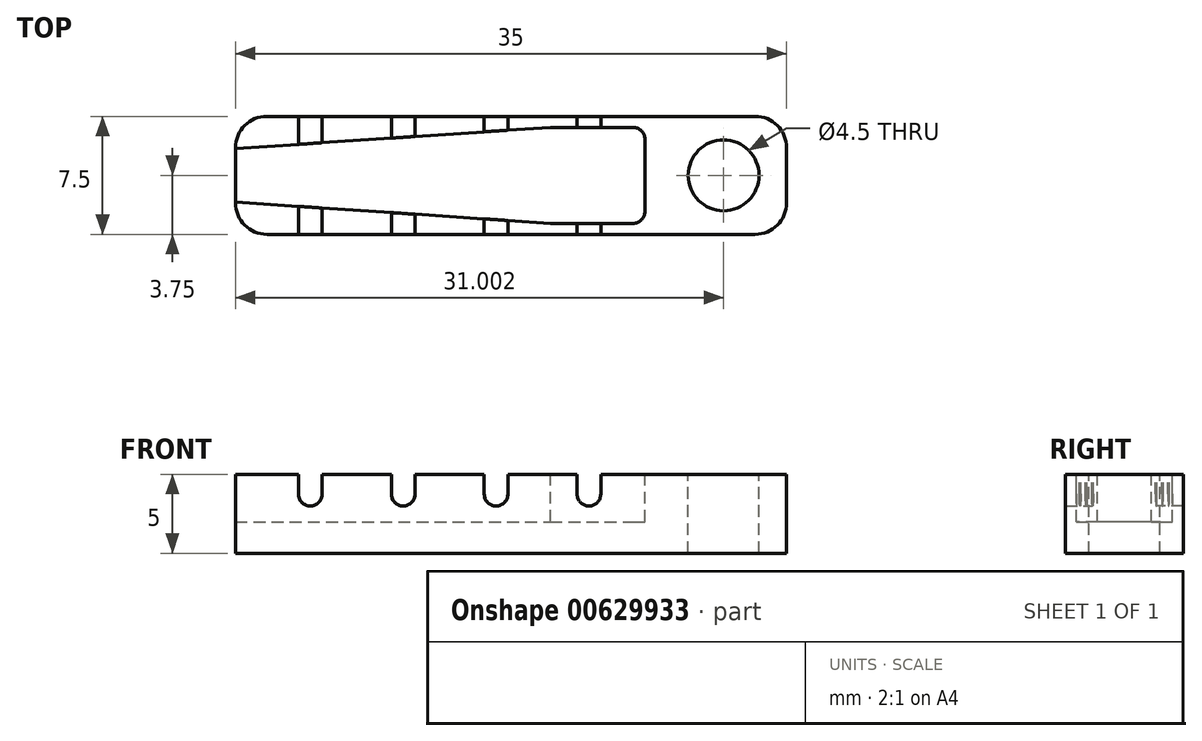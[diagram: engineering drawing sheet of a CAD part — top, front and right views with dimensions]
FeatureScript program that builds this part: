
annotation { "Feature Type Name" : "Feature", "Feature Type Description" : "" }
export const myFeature = defineFeature(function(context is Context, id is Id, definition is map)
    precondition{}
    {
        {
            var Q0;
            Q0=qCreatedBy(makeId("Top.planeOp"),FACE);
            var sketch = newSketch(context, id + "F0", { "sketchPlane" : qUnion([Q0])});
            skLineSegment(sketch, "E0.bottom", {"start": v(-22.89, 3.75) * mm, "end": v(12.11, 3.75) * mm});
            skLineSegment(sketch, "E0.top", {"start": v(-22.89, -3.75) * mm, "end": v(12.11, -3.75) * mm});
            skLineSegment(sketch, "E0.left", {"start": v(-22.89, 3.75) * mm, "end": v(-22.89, -3.75) * mm});
            skLineSegment(sketch, "E0.right", {"start": v(12.11, 3.75) * mm, "end": v(12.11, -3.75) * mm});
            skLineSegment(sketch, "E1", {"start": v(-22.89, 1.7) * mm, "end": v(-2.89, 3.05) * mm});
            skLineSegment(sketch, "E2.MirrorCS", {"start": v(-22.89, -1.7) * mm, "end": v(-2.89, -3.05) * mm});
            skLineSegment(sketch, "E3", {"start": v(-2.89, 3.05) * mm, "end": v(3.11, 3.05) * mm});
            skLineSegment(sketch, "E4.MirrorCS", {"start": v(-2.89, -3.05) * mm, "end": v(3.11, -3.05) * mm});
            skLineSegment(sketch, "E5", {"start": v(3.11, 3.05) * mm, "end": v(3.11, -3.05) * mm});
            skCircle(sketch, "E6", {"center": v(8.11, 0) * mm, "radius": 2.25 * mm});
            skLineSegment(sketch, "E7", {"start": v(-18.89, 3.75) * mm, "end": v(-18.89, -3.75) * mm});
            skLineSegment(sketch, "E8", {"start": v(-17.39, 3.75) * mm, "end": v(-17.39, -3.75) * mm});
            skLineSegment(sketch, "E9.1.0.0", {"start": v(-12.99, 3.75) * mm, "end": v(-12.99, -3.75) * mm});
            skLineSegment(sketch, "E9.1.0.1", {"start": v(-11.49, 3.75) * mm, "end": v(-11.49, -3.75) * mm});
            skLineSegment(sketch, "E9.2.0.0", {"start": v(-7.09, 3.75) * mm, "end": v(-7.09, -3.75) * mm});
            skLineSegment(sketch, "E9.2.0.1", {"start": v(-5.59, 3.75) * mm, "end": v(-5.59, -3.75) * mm});
            skLineSegment(sketch, "E9.3.0.0", {"start": v(-1.19, 3.75) * mm, "end": v(-1.19, -3.75) * mm});
            skLineSegment(sketch, "E9.3.0.1", {"start": v(0.31, 3.75) * mm, "end": v(0.31, -3.75) * mm});
            skLineSegment(sketch, "E9.direction1", {"start": v(-18.89, -3.75) * mm, "end": v(-12.99, -3.75) * mm, "construction": true});
            skSolve(sketch);
        }
        {
            var Q0;
            Q0=qSketchRegion(id+"F0",true);
            var Q1;
            {var subQ0=sQuery(id+"F0.wireOp",EDGE,"E9.3.0.0");var subQ1=sQuery(id+"F0.wireOp",EDGE,"E3");var subQ2=makeQuery(id+"F0.imprint","INTERSECT",VERTEX,{"derivedFrom":[subQ1,subQ0]});Q1=makeQuery(id+"F0.imprint","IMPRINT",FACE,{"disambiguationData":[TD([[makeQuery(id+"F0.imprint","IMPRINT",EDGE,{"disambiguationData":[TD([[subQ2,-1.0]])],"derivedFrom":subQ1}),-1.0]])]});}
            var Q2;
            {var subQ0=sQuery(id+"F0.wireOp",EDGE,"E9.2.0.0");var subQ1=sQuery(id+"F0.wireOp",EDGE,"E1");var subQ2=makeQuery(id+"F0.imprint","INTERSECT",VERTEX,{"derivedFrom":[subQ1,subQ0]});Q2=makeQuery(id+"F0.imprint","IMPRINT",FACE,{"disambiguationData":[TD([[makeQuery(id+"F0.imprint","IMPRINT",EDGE,{"disambiguationData":[TD([[subQ2,-1.0]])],"derivedFrom":subQ1}),-1.0]])]});}
            var Q3;
            {var subQ0=sQuery(id+"F0.wireOp",EDGE,"E7");var subQ1=sQuery(id+"F0.wireOp",EDGE,"E1");var subQ2=makeQuery(id+"F0.imprint","INTERSECT",VERTEX,{"derivedFrom":[subQ1,subQ0]});Q3=makeQuery(id+"F0.imprint","IMPRINT",FACE,{"disambiguationData":[TD([[makeQuery(id+"F0.imprint","IMPRINT",EDGE,{"disambiguationData":[TD([[subQ2,-1.0]])],"derivedFrom":subQ1}),-1.0]])]});}
            var Q4;
            {var subQ0=sQuery(id+"F0.wireOp",EDGE,"E8");var subQ1=sQuery(id+"F0.wireOp",EDGE,"E1");var subQ2=makeQuery(id+"F0.imprint","INTERSECT",VERTEX,{"derivedFrom":[subQ1,subQ0]});Q4=makeQuery(id+"F0.imprint","IMPRINT",FACE,{"disambiguationData":[TD([[makeQuery(id+"F0.imprint","IMPRINT",EDGE,{"disambiguationData":[TD([[subQ2,-1.0]])],"derivedFrom":subQ1}),-1.0]])]});}
            var Q5;
            {var subQ0=sQuery(id+"F0.wireOp",EDGE,"E9.1.0.1");var subQ1=sQuery(id+"F0.wireOp",EDGE,"E1");var subQ2=makeQuery(id+"F0.imprint","INTERSECT",VERTEX,{"derivedFrom":[subQ1,subQ0]});Q5=makeQuery(id+"F0.imprint","IMPRINT",FACE,{"disambiguationData":[TD([[makeQuery(id+"F0.imprint","IMPRINT",EDGE,{"disambiguationData":[TD([[subQ2,-1.0]])],"derivedFrom":subQ1}),-1.0]])]});}
            var Q6;
            {var subQ0=sQuery(id+"F0.wireOp",EDGE,"E9.1.0.0");var subQ1=sQuery(id+"F0.wireOp",EDGE,"E1");var subQ2=makeQuery(id+"F0.imprint","INTERSECT",VERTEX,{"derivedFrom":[subQ1,subQ0]});Q6=makeQuery(id+"F0.imprint","IMPRINT",FACE,{"disambiguationData":[TD([[makeQuery(id+"F0.imprint","IMPRINT",EDGE,{"disambiguationData":[TD([[subQ2,-1.0]])],"derivedFrom":subQ1}),-1.0]])]});}
            var Q7;
            {var subQ5=sQuery(id+"F0.wireOp",EDGE,"E3");var subQ6=sQuery(id+"F0.wireOp",EDGE,"E1");var subQ7=makeQuery(id+"F0.imprint","INTERSECT",VERTEX,{"derivedFrom":[subQ6,subQ5]});Q7=makeQuery(id+"F0.imprint","IMPRINT",FACE,{"disambiguationData":[TD([[makeQuery(id+"F0.imprint","IMPRINT",EDGE,{"disambiguationData":[TD([[subQ7,1.0]])],"derivedFrom":subQ6}),-1.0]])]});}
            var Q8;
            {var subQ0=sQuery(id+"F0.wireOp",EDGE,"E5");Q8=makeQuery(id+"F0.imprint","IMPRINT",FACE,{"disambiguationData":[TD([[makeQuery(id+"F0.imprint","IMPRINT",EDGE,{"derivedFrom":subQ0}),-1.0]])]});}
            extrude(context, id + "F1", {"entities" : qUnion([Q0, Q1, Q2, Q3, Q4, Q5, Q6, Q7, Q8]), "depth" : -5 * mm, "offsetDistance" : 25 * mm});
        }
        {
            var Q0;
            {var subQ0=sQuery(id+"F0.wireOp",EDGE,"E1");var subQ1=sQuery(id+"F0.wireOp",EDGE,"E0.left");var subQ2=makeQuery(id+"F0.imprint","INTERSECT",VERTEX,{"derivedFrom":[subQ1,subQ0]});Q0=makeQuery(id+"F0.imprint","IMPRINT",FACE,{"disambiguationData":[TD([[makeQuery(id+"F0.imprint","IMPRINT",EDGE,{"disambiguationData":[TD([[subQ2,-1.0]])],"derivedFrom":subQ1}),1.0]])]});}
            var Q1;
            {var subQ0=sQuery(id+"F0.wireOp",EDGE,"E7");var subQ1=sQuery(id+"F0.wireOp",EDGE,"E1");var subQ2=makeQuery(id+"F0.imprint","INTERSECT",VERTEX,{"derivedFrom":[subQ1,subQ0]});Q1=makeQuery(id+"F0.imprint","IMPRINT",FACE,{"disambiguationData":[TD([[makeQuery(id+"F0.imprint","IMPRINT",EDGE,{"disambiguationData":[TD([[subQ2,-1.0]])],"derivedFrom":subQ1}),-1.0]])]});}
            var Q2;
            {var subQ0=sQuery(id+"F0.wireOp",EDGE,"E8");var subQ1=sQuery(id+"F0.wireOp",EDGE,"E1");var subQ2=makeQuery(id+"F0.imprint","INTERSECT",VERTEX,{"derivedFrom":[subQ1,subQ0]});Q2=makeQuery(id+"F0.imprint","IMPRINT",FACE,{"disambiguationData":[TD([[makeQuery(id+"F0.imprint","IMPRINT",EDGE,{"disambiguationData":[TD([[subQ2,-1.0]])],"derivedFrom":subQ1}),-1.0]])]});}
            var Q3;
            {var subQ0=sQuery(id+"F0.wireOp",EDGE,"E9.1.0.0");var subQ1=sQuery(id+"F0.wireOp",EDGE,"E1");var subQ2=makeQuery(id+"F0.imprint","INTERSECT",VERTEX,{"derivedFrom":[subQ1,subQ0]});Q3=makeQuery(id+"F0.imprint","IMPRINT",FACE,{"disambiguationData":[TD([[makeQuery(id+"F0.imprint","IMPRINT",EDGE,{"disambiguationData":[TD([[subQ2,-1.0]])],"derivedFrom":subQ1}),-1.0]])]});}
            var Q4;
            {var subQ0=sQuery(id+"F0.wireOp",EDGE,"E9.1.0.1");var subQ1=sQuery(id+"F0.wireOp",EDGE,"E1");var subQ2=makeQuery(id+"F0.imprint","INTERSECT",VERTEX,{"derivedFrom":[subQ1,subQ0]});Q4=makeQuery(id+"F0.imprint","IMPRINT",FACE,{"disambiguationData":[TD([[makeQuery(id+"F0.imprint","IMPRINT",EDGE,{"disambiguationData":[TD([[subQ2,-1.0]])],"derivedFrom":subQ1}),-1.0]])]});}
            var Q5;
            {var subQ0=sQuery(id+"F0.wireOp",EDGE,"E9.2.0.0");var subQ1=sQuery(id+"F0.wireOp",EDGE,"E1");var subQ2=makeQuery(id+"F0.imprint","INTERSECT",VERTEX,{"derivedFrom":[subQ1,subQ0]});Q5=makeQuery(id+"F0.imprint","IMPRINT",FACE,{"disambiguationData":[TD([[makeQuery(id+"F0.imprint","IMPRINT",EDGE,{"disambiguationData":[TD([[subQ2,-1.0]])],"derivedFrom":subQ1}),-1.0]])]});}
            var Q6;
            {var subQ5=sQuery(id+"F0.wireOp",EDGE,"E3");var subQ6=sQuery(id+"F0.wireOp",EDGE,"E1");var subQ7=makeQuery(id+"F0.imprint","INTERSECT",VERTEX,{"derivedFrom":[subQ6,subQ5]});Q6=makeQuery(id+"F0.imprint","IMPRINT",FACE,{"disambiguationData":[TD([[makeQuery(id+"F0.imprint","IMPRINT",EDGE,{"disambiguationData":[TD([[subQ7,1.0]])],"derivedFrom":subQ6}),-1.0]])]});}
            var Q7;
            {var subQ0=sQuery(id+"F0.wireOp",EDGE,"E9.3.0.0");var subQ1=sQuery(id+"F0.wireOp",EDGE,"E3");var subQ2=makeQuery(id+"F0.imprint","INTERSECT",VERTEX,{"derivedFrom":[subQ1,subQ0]});Q7=makeQuery(id+"F0.imprint","IMPRINT",FACE,{"disambiguationData":[TD([[makeQuery(id+"F0.imprint","IMPRINT",EDGE,{"disambiguationData":[TD([[subQ2,-1.0]])],"derivedFrom":subQ1}),-1.0]])]});}
            var Q8;
            {var subQ0=sQuery(id+"F0.wireOp",EDGE,"E5");Q8=makeQuery(id+"F0.imprint","IMPRINT",FACE,{"disambiguationData":[TD([[makeQuery(id+"F0.imprint","IMPRINT",EDGE,{"derivedFrom":subQ0}),-1.0]])]});}
            extrude(context, id + "F2", {"entities" : qUnion([Q0, Q1, Q2, Q3, Q4, Q5, Q6, Q7, Q8]), "operationType" : NewBodyOperationType.REMOVE, "depth" : -3 * mm, "offsetDistance" : 25 * mm});
        }
        {
            var Q0;
            {var subQ0=sQuery(id+"F0.wireOp",EDGE,"E7");var subQ1=sQuery(id+"F0.wireOp",EDGE,"E0.bottom");var subQ2=makeQuery(id+"F0.imprint","INTERSECT",VERTEX,{"derivedFrom":[subQ1,subQ0]});Q0=makeQuery(id+"F0.imprint","IMPRINT",FACE,{"disambiguationData":[TD([[makeQuery(id+"F0.imprint","IMPRINT",EDGE,{"disambiguationData":[TD([[subQ2,-1.0]])],"derivedFrom":subQ1}),-1.0]])]});}
            var Q1;
            {var subQ0=sQuery(id+"F0.wireOp",EDGE,"E9.1.0.0");var subQ1=sQuery(id+"F0.wireOp",EDGE,"E0.bottom");var subQ2=makeQuery(id+"F0.imprint","INTERSECT",VERTEX,{"derivedFrom":[subQ1,subQ0]});Q1=makeQuery(id+"F0.imprint","IMPRINT",FACE,{"disambiguationData":[TD([[makeQuery(id+"F0.imprint","IMPRINT",EDGE,{"disambiguationData":[TD([[subQ2,-1.0]])],"derivedFrom":subQ1}),-1.0]])]});}
            var Q2;
            {var subQ0=sQuery(id+"F0.wireOp",EDGE,"E9.2.0.0");var subQ1=sQuery(id+"F0.wireOp",EDGE,"E0.bottom");var subQ2=makeQuery(id+"F0.imprint","INTERSECT",VERTEX,{"derivedFrom":[subQ1,subQ0]});Q2=makeQuery(id+"F0.imprint","IMPRINT",FACE,{"disambiguationData":[TD([[makeQuery(id+"F0.imprint","IMPRINT",EDGE,{"disambiguationData":[TD([[subQ2,-1.0]])],"derivedFrom":subQ1}),-1.0]])]});}
            var Q3;
            {var subQ0=sQuery(id+"F0.wireOp",EDGE,"E9.3.0.0");var subQ1=sQuery(id+"F0.wireOp",EDGE,"E0.top");var subQ2=makeQuery(id+"F0.imprint","INTERSECT",VERTEX,{"derivedFrom":[subQ1,subQ0]});Q3=makeQuery(id+"F0.imprint","IMPRINT",FACE,{"disambiguationData":[TD([[makeQuery(id+"F0.imprint","IMPRINT",EDGE,{"disambiguationData":[TD([[subQ2,-1.0]])],"derivedFrom":subQ1}),1.0]])]});}
            var Q4;
            {var subQ0=sQuery(id+"F0.wireOp",EDGE,"E7");var subQ1=sQuery(id+"F0.wireOp",EDGE,"E0.top");var subQ2=makeQuery(id+"F0.imprint","INTERSECT",VERTEX,{"derivedFrom":[subQ1,subQ0]});Q4=makeQuery(id+"F0.imprint","IMPRINT",FACE,{"disambiguationData":[TD([[makeQuery(id+"F0.imprint","IMPRINT",EDGE,{"disambiguationData":[TD([[subQ2,-1.0]])],"derivedFrom":subQ1}),1.0]])]});}
            var Q5;
            {var subQ0=sQuery(id+"F0.wireOp",EDGE,"E9.1.0.0");var subQ1=sQuery(id+"F0.wireOp",EDGE,"E0.top");var subQ2=makeQuery(id+"F0.imprint","INTERSECT",VERTEX,{"derivedFrom":[subQ1,subQ0]});Q5=makeQuery(id+"F0.imprint","IMPRINT",FACE,{"disambiguationData":[TD([[makeQuery(id+"F0.imprint","IMPRINT",EDGE,{"disambiguationData":[TD([[subQ2,-1.0]])],"derivedFrom":subQ1}),1.0]])]});}
            var Q6;
            {var subQ0=sQuery(id+"F0.wireOp",EDGE,"E9.2.0.0");var subQ1=sQuery(id+"F0.wireOp",EDGE,"E0.top");var subQ2=makeQuery(id+"F0.imprint","INTERSECT",VERTEX,{"derivedFrom":[subQ1,subQ0]});Q6=makeQuery(id+"F0.imprint","IMPRINT",FACE,{"disambiguationData":[TD([[makeQuery(id+"F0.imprint","IMPRINT",EDGE,{"disambiguationData":[TD([[subQ2,-1.0]])],"derivedFrom":subQ1}),1.0]])]});}
            var Q7;
            {var subQ0=sQuery(id+"F0.wireOp",EDGE,"E9.3.0.0");var subQ1=sQuery(id+"F0.wireOp",EDGE,"E0.bottom");var subQ2=makeQuery(id+"F0.imprint","INTERSECT",VERTEX,{"derivedFrom":[subQ1,subQ0]});Q7=makeQuery(id+"F0.imprint","IMPRINT",FACE,{"disambiguationData":[TD([[makeQuery(id+"F0.imprint","IMPRINT",EDGE,{"disambiguationData":[TD([[subQ2,-1.0]])],"derivedFrom":subQ1}),-1.0]])]});}
            extrude(context, id + "F3", {"entities" : qUnion([Q0, Q1, Q2, Q3, Q4, Q5, Q6, Q7]), "operationType" : NewBodyOperationType.REMOVE, "oppositeDirection" : true, "depth" : 2 * mm, "offsetDistance" : 25 * mm});
        }
        {
            var Q0;
            {var subQ0=sQuery(id+"F0.wireOp",EDGE,"E8");Q0=makeQuery(id+"F3.boolean.opBoolean","COPY",EDGE,{"derivedFrom":makeQuery(id+"F3.opExtrude","CAP_EDGE",EDGE,{"disambiguationData":[OSD([subQ0]),TDD([makeQuery(id+"F0.imprint","IMPRINT",EDGE,{"disambiguationData":[TD([[makeQuery(id+"F0.imprint","INTERSECT",VERTEX,{"derivedFrom":[sQuery(id+"F0.wireOp",EDGE,"E0.top"),subQ0]}),1.0]])],"derivedFrom":subQ0})])],"isStart":false})});}
            var Q1;
            {var subQ0=sQuery(id+"F0.wireOp",EDGE,"E9.1.0.1");Q1=makeQuery(id+"F3.boolean.opBoolean","COPY",EDGE,{"derivedFrom":makeQuery(id+"F3.opExtrude","CAP_EDGE",EDGE,{"disambiguationData":[OSD([subQ0]),TDD([makeQuery(id+"F0.imprint","IMPRINT",EDGE,{"disambiguationData":[TD([[makeQuery(id+"F0.imprint","INTERSECT",VERTEX,{"derivedFrom":[sQuery(id+"F0.wireOp",EDGE,"E0.top"),subQ0]}),1.0]])],"derivedFrom":subQ0})])],"isStart":false})});}
            var Q2;
            {var subQ0=sQuery(id+"F0.wireOp",EDGE,"E9.2.0.1");Q2=makeQuery(id+"F3.boolean.opBoolean","COPY",EDGE,{"derivedFrom":makeQuery(id+"F3.opExtrude","CAP_EDGE",EDGE,{"disambiguationData":[OSD([subQ0]),TDD([makeQuery(id+"F0.imprint","IMPRINT",EDGE,{"disambiguationData":[TD([[makeQuery(id+"F0.imprint","INTERSECT",VERTEX,{"derivedFrom":[sQuery(id+"F0.wireOp",EDGE,"E0.top"),subQ0]}),1.0]])],"derivedFrom":subQ0})])],"isStart":false})});}
            var Q3;
            {var subQ0=sQuery(id+"F0.wireOp",EDGE,"E9.3.0.1");Q3=makeQuery(id+"F3.boolean.opBoolean","COPY",EDGE,{"derivedFrom":makeQuery(id+"F3.opExtrude","CAP_EDGE",EDGE,{"disambiguationData":[OSD([subQ0]),TDD([makeQuery(id+"F0.imprint","IMPRINT",EDGE,{"disambiguationData":[TD([[makeQuery(id+"F0.imprint","INTERSECT",VERTEX,{"derivedFrom":[sQuery(id+"F0.wireOp",EDGE,"E0.top"),subQ0]}),1.0]])],"derivedFrom":subQ0})])],"isStart":false})});}
            var Q4;
            {var subQ0=sQuery(id+"F0.wireOp",EDGE,"E7");Q4=makeQuery(id+"F3.boolean.opBoolean","COPY",EDGE,{"derivedFrom":makeQuery(id+"F3.opExtrude","CAP_EDGE",EDGE,{"disambiguationData":[OSD([subQ0]),TDD([makeQuery(id+"F0.imprint","IMPRINT",EDGE,{"disambiguationData":[TD([[makeQuery(id+"F0.imprint","INTERSECT",VERTEX,{"derivedFrom":[sQuery(id+"F0.wireOp",EDGE,"E0.top"),subQ0]}),1.0]])],"derivedFrom":subQ0})])],"isStart":false})});}
            var Q5;
            {var subQ0=sQuery(id+"F0.wireOp",EDGE,"E9.1.0.0");Q5=makeQuery(id+"F3.boolean.opBoolean","COPY",EDGE,{"derivedFrom":makeQuery(id+"F3.opExtrude","CAP_EDGE",EDGE,{"disambiguationData":[OSD([subQ0]),TDD([makeQuery(id+"F0.imprint","IMPRINT",EDGE,{"disambiguationData":[TD([[makeQuery(id+"F0.imprint","INTERSECT",VERTEX,{"derivedFrom":[sQuery(id+"F0.wireOp",EDGE,"E0.top"),subQ0]}),1.0]])],"derivedFrom":subQ0})])],"isStart":false})});}
            var Q6;
            {var subQ0=sQuery(id+"F0.wireOp",EDGE,"E9.2.0.0");Q6=makeQuery(id+"F3.boolean.opBoolean","COPY",EDGE,{"derivedFrom":makeQuery(id+"F3.opExtrude","CAP_EDGE",EDGE,{"disambiguationData":[OSD([subQ0]),TDD([makeQuery(id+"F0.imprint","IMPRINT",EDGE,{"disambiguationData":[TD([[makeQuery(id+"F0.imprint","INTERSECT",VERTEX,{"derivedFrom":[sQuery(id+"F0.wireOp",EDGE,"E0.top"),subQ0]}),1.0]])],"derivedFrom":subQ0})])],"isStart":false})});}
            var Q7;
            {var subQ0=sQuery(id+"F0.wireOp",EDGE,"E9.3.0.0");Q7=makeQuery(id+"F3.boolean.opBoolean","COPY",EDGE,{"derivedFrom":makeQuery(id+"F3.opExtrude","CAP_EDGE",EDGE,{"disambiguationData":[OSD([subQ0]),TDD([makeQuery(id+"F0.imprint","IMPRINT",EDGE,{"disambiguationData":[TD([[makeQuery(id+"F0.imprint","INTERSECT",VERTEX,{"derivedFrom":[sQuery(id+"F0.wireOp",EDGE,"E0.top"),subQ0]}),1.0]])],"derivedFrom":subQ0})])],"isStart":false})});}
            var Q8;
            {var subQ0=sQuery(id+"F0.wireOp",EDGE,"E7");Q8=makeQuery(id+"F3.boolean.opBoolean","COPY",EDGE,{"derivedFrom":makeQuery(id+"F3.opExtrude","CAP_EDGE",EDGE,{"disambiguationData":[OSD([subQ0]),TDD([makeQuery(id+"F0.imprint","IMPRINT",EDGE,{"disambiguationData":[TD([[makeQuery(id+"F0.imprint","INTERSECT",VERTEX,{"derivedFrom":[sQuery(id+"F0.wireOp",EDGE,"E0.bottom"),subQ0]}),-1.0]])],"derivedFrom":subQ0})])],"isStart":false})});}
            var Q9;
            {var subQ0=sQuery(id+"F0.wireOp",EDGE,"E9.1.0.0");Q9=makeQuery(id+"F3.boolean.opBoolean","COPY",EDGE,{"derivedFrom":makeQuery(id+"F3.opExtrude","CAP_EDGE",EDGE,{"disambiguationData":[OSD([subQ0]),TDD([makeQuery(id+"F0.imprint","IMPRINT",EDGE,{"disambiguationData":[TD([[makeQuery(id+"F0.imprint","INTERSECT",VERTEX,{"derivedFrom":[sQuery(id+"F0.wireOp",EDGE,"E0.bottom"),subQ0]}),-1.0]])],"derivedFrom":subQ0})])],"isStart":false})});}
            var Q10;
            {var subQ0=sQuery(id+"F0.wireOp",EDGE,"E9.2.0.0");Q10=makeQuery(id+"F3.boolean.opBoolean","COPY",EDGE,{"derivedFrom":makeQuery(id+"F3.opExtrude","CAP_EDGE",EDGE,{"disambiguationData":[OSD([subQ0]),TDD([makeQuery(id+"F0.imprint","IMPRINT",EDGE,{"disambiguationData":[TD([[makeQuery(id+"F0.imprint","INTERSECT",VERTEX,{"derivedFrom":[sQuery(id+"F0.wireOp",EDGE,"E0.bottom"),subQ0]}),-1.0]])],"derivedFrom":subQ0})])],"isStart":false})});}
            var Q11;
            {var subQ0=sQuery(id+"F0.wireOp",EDGE,"E9.3.0.0");Q11=makeQuery(id+"F3.boolean.opBoolean","COPY",EDGE,{"derivedFrom":makeQuery(id+"F3.opExtrude","CAP_EDGE",EDGE,{"disambiguationData":[OSD([subQ0]),TDD([makeQuery(id+"F0.imprint","IMPRINT",EDGE,{"disambiguationData":[TD([[makeQuery(id+"F0.imprint","INTERSECT",VERTEX,{"derivedFrom":[sQuery(id+"F0.wireOp",EDGE,"E0.bottom"),subQ0]}),-1.0]])],"derivedFrom":subQ0})])],"isStart":false})});}
            var Q12;
            {var subQ0=sQuery(id+"F0.wireOp",EDGE,"E8");Q12=makeQuery(id+"F3.boolean.opBoolean","COPY",EDGE,{"derivedFrom":makeQuery(id+"F3.opExtrude","CAP_EDGE",EDGE,{"disambiguationData":[OSD([subQ0]),TDD([makeQuery(id+"F0.imprint","IMPRINT",EDGE,{"disambiguationData":[TD([[makeQuery(id+"F0.imprint","INTERSECT",VERTEX,{"derivedFrom":[sQuery(id+"F0.wireOp",EDGE,"E0.bottom"),subQ0]}),-1.0]])],"derivedFrom":subQ0})])],"isStart":false})});}
            var Q13;
            {var subQ0=sQuery(id+"F0.wireOp",EDGE,"E9.1.0.1");Q13=makeQuery(id+"F3.boolean.opBoolean","COPY",EDGE,{"derivedFrom":makeQuery(id+"F3.opExtrude","CAP_EDGE",EDGE,{"disambiguationData":[OSD([subQ0]),TDD([makeQuery(id+"F0.imprint","IMPRINT",EDGE,{"disambiguationData":[TD([[makeQuery(id+"F0.imprint","INTERSECT",VERTEX,{"derivedFrom":[sQuery(id+"F0.wireOp",EDGE,"E0.bottom"),subQ0]}),-1.0]])],"derivedFrom":subQ0})])],"isStart":false})});}
            var Q14;
            {var subQ0=sQuery(id+"F0.wireOp",EDGE,"E9.2.0.1");Q14=makeQuery(id+"F3.boolean.opBoolean","COPY",EDGE,{"derivedFrom":makeQuery(id+"F3.opExtrude","CAP_EDGE",EDGE,{"disambiguationData":[OSD([subQ0]),TDD([makeQuery(id+"F0.imprint","IMPRINT",EDGE,{"disambiguationData":[TD([[makeQuery(id+"F0.imprint","INTERSECT",VERTEX,{"derivedFrom":[sQuery(id+"F0.wireOp",EDGE,"E0.bottom"),subQ0]}),-1.0]])],"derivedFrom":subQ0})])],"isStart":false})});}
            var Q15;
            {var subQ0=sQuery(id+"F0.wireOp",EDGE,"E9.3.0.1");Q15=makeQuery(id+"F3.boolean.opBoolean","COPY",EDGE,{"derivedFrom":makeQuery(id+"F3.opExtrude","CAP_EDGE",EDGE,{"disambiguationData":[OSD([subQ0]),TDD([makeQuery(id+"F0.imprint","IMPRINT",EDGE,{"disambiguationData":[TD([[makeQuery(id+"F0.imprint","INTERSECT",VERTEX,{"derivedFrom":[sQuery(id+"F0.wireOp",EDGE,"E0.bottom"),subQ0]}),-1.0]])],"derivedFrom":subQ0})])],"isStart":false})});}
            var Q16;
            Q16=makeQuery(id+"F2.boolean.opBoolean","COPY",EDGE,{"derivedFrom":makeQuery(id+"F2.opExtrude","SWEPT_EDGE",EDGE,{"disambiguationData":[OSD([sQuery(id+"F0.wireOp",EDGE,"E3"),sQuery(id+"F0.wireOp",EDGE,"E5")])]})});
            var Q17;
            Q17=makeQuery(id+"F2.boolean.opBoolean","COPY",EDGE,{"derivedFrom":makeQuery(id+"F2.opExtrude","SWEPT_EDGE",EDGE,{"disambiguationData":[OSD([sQuery(id+"F0.wireOp",EDGE,"E4.MirrorCS"),sQuery(id+"F0.wireOp",EDGE,"E5")])]})});
            fillet(context, id + "F4", {"entities" : qUnion([Q0, Q1, Q2, Q3, Q4, Q5, Q6, Q7, Q8, Q9, Q10, Q11, Q12, Q13, Q14, Q15, Q16, Q17]), "radius" : .75 * mm, "tangentPropagation" : true, "allowEdgeOverflow" : false});
        }
        {
            var Q0;
            Q0=makeQuery(id+"F1.opExtrude","SWEPT_EDGE",EDGE,{"disambiguationData":[OSD([sQuery(id+"F0.wireOp",EDGE,"E0.top"),sQuery(id+"F0.wireOp",EDGE,"E0.left")])]});
            var Q1;
            Q1=makeQuery(id+"F1.opExtrude","SWEPT_EDGE",EDGE,{"disambiguationData":[OSD([sQuery(id+"F0.wireOp",EDGE,"E0.bottom"),sQuery(id+"F0.wireOp",EDGE,"E0.left")])]});
            var Q2;
            Q2=makeQuery(id+"F1.opExtrude","SWEPT_EDGE",EDGE,{"disambiguationData":[OSD([sQuery(id+"F0.wireOp",EDGE,"E0.top"),sQuery(id+"F0.wireOp",EDGE,"E0.right")])]});
            var Q3;
            Q3=makeQuery(id+"F1.opExtrude","SWEPT_EDGE",EDGE,{"disambiguationData":[OSD([sQuery(id+"F0.wireOp",EDGE,"E0.bottom"),sQuery(id+"F0.wireOp",EDGE,"E0.right")])]});
            fillet(context, id + "F5", {"entities" : qUnion([Q0, Q1, Q2, Q3]), "radius" : 2 * mm, "tangentPropagation" : true, "allowEdgeOverflow" : false});
        }
    });
